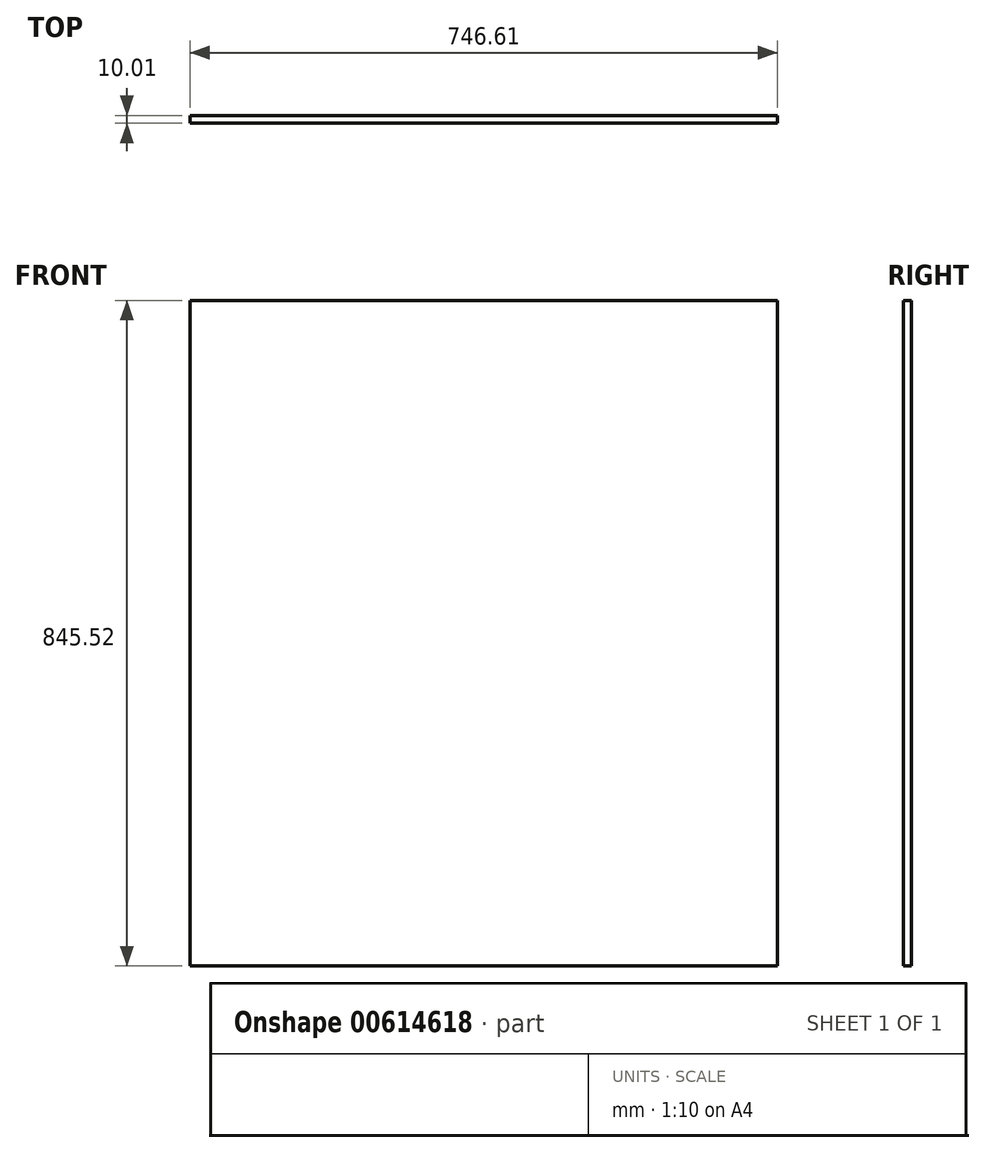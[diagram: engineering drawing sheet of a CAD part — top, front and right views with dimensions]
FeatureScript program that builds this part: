
annotation { "Feature Type Name" : "Feature", "Feature Type Description" : "" }
export const myFeature = defineFeature(function(context is Context, id is Id, definition is map)
    precondition{}
    {
        {
            var Q0;
            Q0=qCreatedBy(makeId("Front.planeOp"),FACE);
            var sketch = newSketch(context, id + "F0", { "sketchPlane" : qUnion([Q0])});
            skLineSegment(sketch, "E0.bottom", {"start": v(0, 0) * mm, "end": v(746.6, 0) * mm});
            skLineSegment(sketch, "E0.top", {"start": v(0, 845.52) * mm, "end": v(746.6, 845.52) * mm});
            skLineSegment(sketch, "E0.left", {"start": v(0, 0) * mm, "end": v(0, 845.52) * mm});
            skLineSegment(sketch, "E0.right", {"start": v(746.6, 0) * mm, "end": v(746.6, 845.52) * mm});
            skSolve(sketch);
        }
        {
            var Q0;
            Q0=makeQuery(id+"F0.imprint","IMPRINT",FACE,{"disambiguationData":[TD([[makeQuery(id+"F0.imprint","IMPRINT",EDGE,{"derivedFrom":sQuery(id+"F0.wireOp",EDGE,"E0.bottom")}),1.0]])]});
            extrude(context, id + "F1", {"entities" : qUnion([Q0]), "depth" : 10 * mm, "offsetDistance" : 25.4 * mm});
        }
    });
